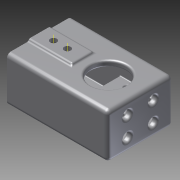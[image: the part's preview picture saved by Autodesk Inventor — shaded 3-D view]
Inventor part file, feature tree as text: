
AUTODESK INVENTOR PART (.ipt)
format: ipt  version: 2012 (Build 160160000, 160)  size: 1,040,896 bytes
history: native  units: mm
features: extrude x30, sketch x30, fillet x15, reference x11, projected_geometry x11, other x4
ambient origin geometry x8: Origin, YZ Plane, XZ Plane, XY Plane, X Axis, Y Axis, Z Axis, Center Point
bodies: Solid1 (feature_tree)
feature tree (101):
  extrude  "Extrusion1"  Depth=2.0mm
  extrude  "Extrusion2"  Depth=2.0mm
  extrude  "Extrusion4"  Depth=3.0mm
  extrude  "Extrusion5"  Depth=3.0mm
  extrude  "Extrusion6"  Depth=0.3mm
  extrude  "Extrusion7"  Depth=0.3mm
  fillet  "Fillet1"  Radius=0.7mm
  extrude  "Extrusion8"  Depth=3.0mm
  extrude  "Extrusion9"  Depth=3.0mm
  extrude  "Extrusion10"  Depth=2.3mm TaperAngle=0.0deg
  extrude  "Extrusion11"  Depth=0.7mm TaperAngle=0.0deg
  other  "Work Axis1"
  extrude  "Extrusion12"  Depth=0.5mm
  extrude  "Extrusion13"  Depth=20.0mm TaperAngle=0.0deg
  extrude  "Extrusion15"  Depth=0.3mm
  other  "Work Axis3"
  extrude  "Extrusion16"  Depth=4.0mm
  extrude  "Extrusion17"  Depth=1.0mm TaperAngle=0.0deg
  extrude  "Extrusion18"  Depth=10.0mm TaperAngle=0.0deg
  extrude  "Extrusion19"  Depth=10.0mm TaperAngle=0.0deg
  extrude  "Extrusion20"  Depth=10.0mm TaperAngle=0.0deg
  fillet  "Fillet3"  Radius=25.903503mm
  fillet  "Fillet4"  Radius=12.951751mm
  fillet  "Fillet5"  Radius=5.0mm
  extrude  "Extrusion21"  Depth=31.903503mm
  extrude  "Extrusion22"  Depth=10.6mm
  extrude  "Extrusion23"  Depth=3.3mm
  extrude  "Extrusion24"  Depth=5.509188mm
  fillet  "Fillet10"  Radius=1.695406mm
  extrude  "Extrusion25"  Depth=1.695406mm
  extrude  "Extrusion26"  Depth=0.6mm TaperAngle=0.0deg
  extrude  "Extrusion27"  Depth=2.0mm
  fillet  "Fillet12"  Radius=3.333333mm
  fillet  "Fillet13"  Radius=10.0mm
  fillet  "Fillet17"  Radius=20.0mm
  extrude  "Extrusion28"  Depth=1.25mm
  fillet  "Fillet18"  Radius=2.5mm
  extrude  "Extrusion29"  Depth=19.403503mm
  fillet  "Fillet19"  Radius=6.467834mm
  fillet  "Fillet20"  Radius=6.467834mm
  fillet  "Fillet21"  Radius=6.467834mm
  fillet  "Fillet22"  Radius=3.333333mm
  extrude  "Extrusion30"  Depth=7.0mm
  other  "Work Axis4"
  other  "Work Axis5"
  extrude  "Extrusion31"  Depth=10.0mm TaperAngle=0.0deg
  fillet  "Fillet23"  Radius=13.2mm
  extrude  "Extrusion32"  Depth=0.5mm
  fillet  "Fillet25"  Radius=0.4mm
  sketch  "Sketch1"  dims[d0=2.0mm d1=2.0mm]
  reference  "Reference1"
  reference  "Reference3"
  reference  "Reference4"
  sketch  "Sketch2"  dims[d2=2.0mm d3=2.0mm]
  sketch  "Sketch3"  dims[d4=3.0mm d5=3.0mm]
  sketch  "Sketch4"  dims[d6=3.0mm d7=3.0mm]
  reference  "Reference6"
  sketch  "Sketch5"  dims[d8=3.0mm d9=0.0mm d10=0.3mm]
  projected_geometry  "Projected Loop1"
  sketch  "Sketch6"  dims[d11=0.3mm d12=0.3mm d14=0.7mm d15=0.0mm]
  sketch  "Sketch7"  dims[d17=3.0mm d18=3.0mm]
  projected_geometry  "Projected Loop2"
  reference  "Reference7"
  reference  "Reference8"
  reference  "Reference9"
  reference  "Reference10"
  sketch  "Sketch8"  dims[d19=3.0mm d20=3.0mm]
  sketch  "Sketch9"  dims[d23=16.0mm d24=0.0mm d26=2.3mm d27=0.0mm]
  reference  "Reference12"
  reference  "Reference13"
  sketch  "Sketch10"  dims[d28=2.0mm d29=0.0mm d30=0.7mm d31=0.0mm]
  reference  "Reference14"
  projected_geometry  "Projected Loop3"
  sketch  "Sketch11"  dims[d32=2.0mm d33=0.5mm]
  sketch  "Sketch12"  dims[d34=0.5mm d35=20.0mm d36=0.0mm]
  sketch  "Sketch15"  dims[d38=1.0mm d39=0.0mm d40=0.3mm]
  sketch  "Sketch16"  dims[d41=1.0mm d42=0.0mm d44=4.0mm]
  sketch  "Sketch17"  dims[d45=4.0mm d46=1.0mm d47=0.0mm]
  sketch  "Sketch18"  dims[d48=10.9mm d49=10.0mm d50=0.0mm]
  sketch  "Sketch19"  dims[d51=1.5mm d52=10.0mm d53=0.0mm]
  sketch  "Sketch20"  dims[d57=12.8mm d58=10.0mm d59=0.0mm d60=25.903503mm d61=12.951751mm d62=5.0mm]
  sketch  "Sketch21"  dims[d63=5.3mm d64=31.903503mm]
  projected_geometry  "Projected Loop4"
  sketch  "Sketch22"  dims[d66=15.951751mm d67=10.6mm]
  projected_geometry  "Projected Loop5"
  sketch  "Sketch24"  dims[d68=10.9mm d69=3.3mm]
  projected_geometry  "Projected Loop6"
  projected_geometry  "Projected Loop7"
  sketch  "Sketch25"  dims[d70=8.9mm d71=5.509188mm d72=1.695406mm]
  sketch  "Sketch26"  dims[d73=1.695406mm d74=1.695406mm]
  projected_geometry  "Projected Loop8"
  sketch  "Sketch27"  dims[d75=10.0mm d76=0.0mm d77=0.6mm d78=0.0mm]
  projected_geometry  "Projected Loop9"
  sketch  "Sketch28"  dims[d79=2.5mm d80=2.0mm d81=3.333333mm d82=10.0mm d83=20.0mm]
  projected_geometry  "Projected Loop10"
  sketch  "Sketch29"  dims[d84=10.0mm d85=0.0mm d86=1.25mm d88=2.5mm]
  sketch  "Sketch30"  dims[d89=2.5mm d90=19.403503mm d91=6.467834mm d92=6.467834mm d93=6.467834mm d94=3.333333mm]
  projected_geometry  "Projected Loop11"
  sketch  "Sketch31"  dims[d95=3.333333mm d96=7.0mm]
  sketch  "Sketch32"  dims[d97=16.7mm d98=10.0mm d99=0.0mm d100=13.2mm]
  sketch  "Sketch33"  dims[d101=10.0mm d102=0.0mm d104=0.5mm d105=0.4mm d106=0.4mm d107=1.0mm d108=1.0mm d109=1.0mm d110=1.0mm d111=0.0mm d112=1.0mm d113=0.0mm d122=25.103503mm d127=4.25mm d128=4.25mm d129=4.25mm d130=4.25mm d131=4.25mm d132=1.0mm d133=0.0mm d135=12.551751mm d136=4.0mm d138=6.275876mm d139=6.275876mm d140=12.551751mm d141=1.0mm d142=0.0mm d143=1.0mm d145=3.64mm d146=0.0mm d147=1.0mm d148=1.0mm d149=1.0mm d150=0.0mm d151=1.0mm d152=0.0mm d153=1.0mm d154=1.0mm d158=0.5mm d159=1.5mm d160=0.0mm d161=0.5mm d162=1.5mm d163=0.0mm d164=0.5mm d165=0.5mm d166=0.5mm d167=0.5mm d168=3.2mm d169=3.2mm d170=6.832425mm d171=9.435898mm d172=20.497274mm d173=4.717949mm d174=4.717949mm d175=6.832425mm d176=1.5mm d177=0.0mm d178=13.5mm d179=10.0mm d180=0.0mm d181=1.0mm d183=0.2mm d184=10.0mm d185=0.0mm d186=1.0mm]
